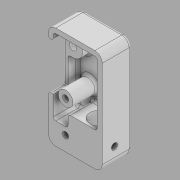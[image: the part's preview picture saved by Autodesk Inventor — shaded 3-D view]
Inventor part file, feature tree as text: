
AUTODESK INVENTOR PART (.ipt)
format: ipt  version: 2020 (Build 240168000, 168)  size: 378,880 bytes
history: native  units: in
note: dims shown in document units (in); Inventor stores cm internally (conversion verified against a paired STEP export)
features: sketch x10, projected_geometry x8, extrude x5, hole x5, fillet x4
ambient origin geometry x8: Origin, YZ Plane, XZ Plane, XY Plane, X Axis, Y Axis, Z Axis, Center Point
bodies: Solid1 (feature_tree)
feature tree (32):
  extrude  "Extrusion1"  Depth=2.75in
  extrude  "Extrusion2"  Depth=1.5in TaperAngle=0.0deg
  extrude  "Extrusion3"  Depth=0.25in
  extrude  "Extrusion4"  Depth=1.5in
  extrude  "Extrusion5"  Depth=1.25in TaperAngle=0.0deg
  hole  "Hole1"  [1 undecoded]
  fillet  "Fillet1"  Radius=0.625in
  fillet  "Fillet2"  Radius=0.125in
  fillet  "Fillet3"  Radius=0.25in
  fillet  "Fillet4"  Radius=1.0in
  hole  "Hole2"  [1 undecoded]
  hole  "Hole6"  [1 undecoded]
  hole  "Hole7"  [1 undecoded]
  hole  "Hole8"  [1 undecoded]
  sketch  "Sketch1"  dims[d0=5.25in d1=2.75in]
  sketch  "Sketch2"  dims[d2=0.375in d3=1.5in d4=0.0in]
  projected_geometry  "Projected Loop1"
  sketch  "Sketch3"  dims[d5=0.25in d6=0.25in]
  projected_geometry  "Projected Loop2"
  sketch  "Sketch4"  dims[d7=1.5in d8=0.625in]
  projected_geometry  "Projected Loop3"
  projected_geometry  "Projected Loop4"
  projected_geometry  "Projected Loop5"
  sketch  "Sketch5"  dims[d9=1.75in d10=1.25in d11=0.0in]
  projected_geometry  "Projected Loop6"
  projected_geometry  "Projected Loop7"
  sketch  "Sketch6"  dims[d12=0.75in d13=2.375in d14=0.625in d15=0.125in d16=0.25in d17=0.0in d18=1.0in]
  sketch  "Sketch7"  dims[d19=4.125in d20=0.5in]
  projected_geometry  "Projected Loop8"
  sketch  "Sketch11"  dims[d23=0.5in d24=0.0in d25=0.75in]
  sketch  "Sketch12"  dims[d26=2.375in d27=0.875in]
  sketch  "Sketch13"  dims[d28=1.25in d29=0.0in d30=0.75in d31=0.625in d32=1.0in d33=0.276in d34=0.375in d35=0.25in d36=0.5635in d37=0.181in d38=0.8108in d39=0.125in d40=0.125in d41=0.125in d42=0.125in d43=0.375in d44=0.276in d45=0.375in d46=0.25in d47=0.5635in d48=0.181in d49=0.8108in d75=0.625in d76=0.875in d77=0.3125in d78=0.75in d79=0.75in d80=0.188in d81=0.5635in d82=0.6in d83=0.0in d86=0.875in d87=2.375in d88=0.3125in d89=0.75in d90=0.5in d91=0.3125in d92=0.5635in d93=0.6in d94=0.0in d95=0.875in d96=0.75in d97=0.3125in d98=0.75in d99=0.5in d100=0.3125in d101=0.5635in d102=0.6in d103=0.0in]
note: 5 required parameter values undecoded (feature->parameter linkage not recoverable at this tier; creation-order binding heuristic only, values carry confidence <= 0.55)
